# Revit family: 712-0220-001-DN300
name_source: partatom
category: Pipe Fittings
units: mm (PartAtom-declared; Revit-internal decimal feet)

## family parameters
Always vertical = Yes
Cut with Voids When Loaded = No
Part Type = Elbow
Round Connector Dimension = Use Diameter
Shared = No
Work Plane-Based = No

## types (1)
- DN300_PN10/16
    A = 22.50°
    Body_wallthickness = 315 mm  [stored 1.03346 ft]
    DN300_PN10 = 712-0300-02-200
    DN300_PN10/16 = Yes
    DN300_PN16 = 712-0300-02-201
    Description_ = AVK FLANGED BEND 22.5° W/LOOSE FLANGES
    FOD = 228 mm
    Flange_thickness = 29 mm  [stored 0.0951444 ft]
    ID(Radius) = 150 mm  [stored 0.492126 ft]
    L = 210 mm  [stored 0.688976 ft]
    L_Ref = 130 mm  [stored 0.426509 ft]
    Nominal Diameter(DN) = 300 mm  [stored 0.984252 ft]
    RF_Thick = 4 mm  [stored 0.0131234 ft]
    Rf_Dia = 185 mm  [stored 0.606955 ft]
    URL product pages = https://www.avkvalves.com

note: [stored X ft] marks values corroborated as IEEE doubles in the binary element streams (Revit-internal decimal feet)

## geometry (parser evidence)
native form markers: Sweep x19
no freeform markers — native parametric forms only
